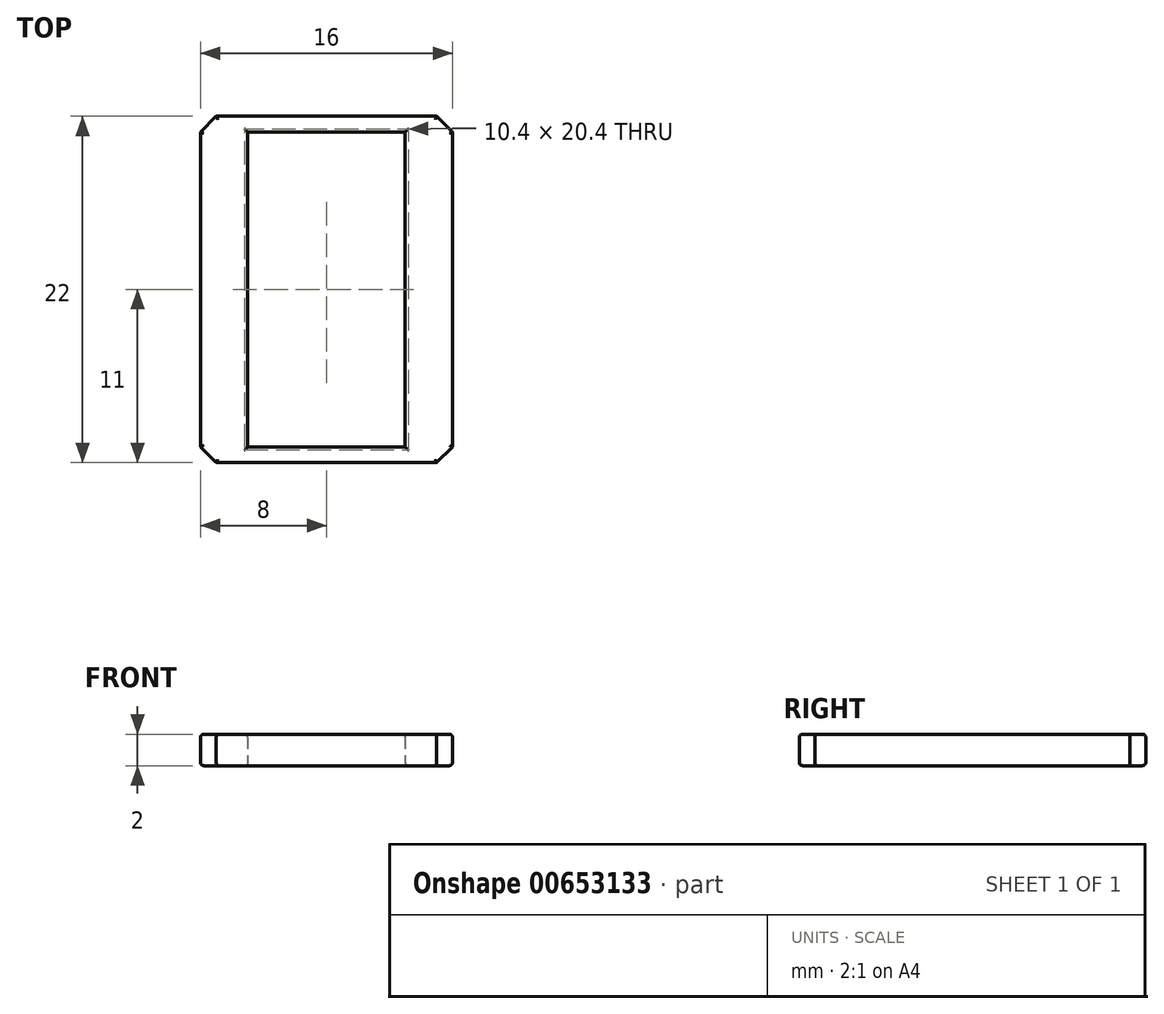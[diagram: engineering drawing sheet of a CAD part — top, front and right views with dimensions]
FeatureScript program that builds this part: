
annotation { "Feature Type Name" : "Feature", "Feature Type Description" : "" }
export const myFeature = defineFeature(function(context is Context, id is Id, definition is map)
    precondition{}
    {
        {
            var Q0;
            Q0=qCreatedBy(makeId("Top.planeOp"),FACE);
            var sketch = newSketch(context, id + "F0", { "sketchPlane" : qUnion([Q0])});
            skLineSegment(sketch, "E0.bottom", {"start": v(-8, 11) * mm, "end": v(8, 11) * mm});
            skLineSegment(sketch, "E0.top", {"start": v(-8, -11) * mm, "end": v(8, -11) * mm});
            skLineSegment(sketch, "E0.left", {"start": v(-8, 11) * mm, "end": v(-8, -11) * mm});
            skLineSegment(sketch, "E0.right", {"start": v(8, 11) * mm, "end": v(8, -11) * mm});
            skPoint(sketch, "E0.middle", {"position": v(0, 0) * mm});
            skSolve(sketch);
        }
        {
            var Q0;
            Q0=makeQuery(id+"F0.imprint","IMPRINT",FACE,{"disambiguationData":[TD([[makeQuery(id+"F0.imprint","IMPRINT",EDGE,{"derivedFrom":sQuery(id+"F0.wireOp",EDGE,"E0.bottom")}),-1.0]])]});
            var sketch = newSketch(context, id + "F1", { "sketchPlane" : qUnion([Q0])});
            skLineSegment(sketch, "E1.bottom", {"start": v(-5, 10) * mm, "end": v(5, 10) * mm});
            skLineSegment(sketch, "E1.top", {"start": v(-5, -10) * mm, "end": v(5, -10) * mm});
            skLineSegment(sketch, "E1.left", {"start": v(-5, 10) * mm, "end": v(-5, -10) * mm});
            skLineSegment(sketch, "E1.right", {"start": v(5, 10) * mm, "end": v(5, -10) * mm});
            skPoint(sketch, "E1.middle", {"position": v(0, 0) * mm});
            skSolve(sketch);
        }
        {
            var Q0;
            Q0=makeQuery(id+"F1.imprint","IMPRINT",FACE,{"disambiguationData":[TD([[makeQuery(id+"F1.imprint","IMPRINT",EDGE,{"derivedFrom":sQuery(id+"F1.wireOp",EDGE,"E1.bottom")}),1.0]])]});
            extrude(context, id + "F2", {"entities" : qUnion([Q0]), "depth" : 2 * mm, "offsetDistance" : 25 * mm});
        }
        {
            var Q0;
            Q0=makeQuery(id+"F2.opExtrude","SWEPT_EDGE",EDGE,{"disambiguationData":[OSD([sQuery(id+"F0.wireOp",EDGE,"E0.top"),sQuery(id+"F0.wireOp",EDGE,"E0.left")])]});
            chamfer(context, id + "F3", {"entities" : qUnion([Q0]), "chamferType" : ChamferType.TWO_OFFSETS, "width1" : 1 * mm, "oppositeDirection" : false, "width2" : 1 * mm, "tangentPropagation" : true});
        }
        {
            var Q0;
            Q0=makeQuery(id+"F2.opExtrude","SWEPT_EDGE",EDGE,{"disambiguationData":[OSD([sQuery(id+"F0.wireOp",EDGE,"E0.top"),sQuery(id+"F0.wireOp",EDGE,"E0.right")])]});
            var Q1;
            Q1=makeQuery(id+"F2.opExtrude","SWEPT_EDGE",EDGE,{"disambiguationData":[OSD([sQuery(id+"F0.wireOp",EDGE,"E0.bottom"),sQuery(id+"F0.wireOp",EDGE,"E0.right")])]});
            var Q2;
            Q2=makeQuery(id+"F2.opExtrude","SWEPT_EDGE",EDGE,{"disambiguationData":[OSD([sQuery(id+"F0.wireOp",EDGE,"E0.bottom"),sQuery(id+"F0.wireOp",EDGE,"E0.left")])]});
            chamfer(context, id + "F4", {"entities" : qUnion([Q0, Q1, Q2]), "chamferType" : ChamferType.TWO_OFFSETS, "width1" : 1 * mm, "oppositeDirection" : false, "width2" : 1 * mm, "tangentPropagation" : true});
        }
        {
            var Q0;
            Q0=makeQuery(id+"F2.opExtrude","CAP_FACE",FACE,{"disambiguationData":[OSD([sQuery(id+"F0.wireOp",EDGE,"E0.bottom"),sQuery(id+"F0.wireOp",EDGE,"E0.top"),sQuery(id+"F0.wireOp",EDGE,"E0.left"),sQuery(id+"F0.wireOp",EDGE,"E0.right"),sQuery(id+"F1.wireOp",EDGE,"E1.bottom"),sQuery(id+"F1.wireOp",EDGE,"E1.top"),sQuery(id+"F1.wireOp",EDGE,"E1.left"),sQuery(id+"F1.wireOp",EDGE,"E1.right")])],"isStart":false});
            var Q1;
            Q1=makeQuery(id+"F2.opExtrude","CAP_FACE",FACE,{"disambiguationData":[OSD([sQuery(id+"F0.wireOp",EDGE,"E0.bottom"),sQuery(id+"F0.wireOp",EDGE,"E0.top"),sQuery(id+"F0.wireOp",EDGE,"E0.left"),sQuery(id+"F0.wireOp",EDGE,"E0.right"),sQuery(id+"F1.wireOp",EDGE,"E1.bottom"),sQuery(id+"F1.wireOp",EDGE,"E1.top"),sQuery(id+"F1.wireOp",EDGE,"E1.left"),sQuery(id+"F1.wireOp",EDGE,"E1.right")])],"isStart":true});
            fillet(context, id + "F5", {"entities" : qUnion([Q0, Q1]), "tangentPropagation" : true, "radius" : 0.2 * mm, "defaultsChanged" : true, "vertexSettings" : [], "allowEdgeOverflow" : false});
        }
    });
